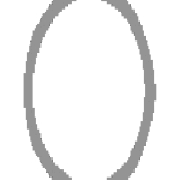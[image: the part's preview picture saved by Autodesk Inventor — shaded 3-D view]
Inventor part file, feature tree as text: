
AUTODESK INVENTOR PART (.ipt)
format: ipt  version: 2021 (Build 250183000, 183)  size: 110,080 bytes
history: native  units: in
note: dims shown in document units (in); Inventor stores cm internally (conversion verified against a paired STEP export)
features: other x4, sketch x3, plane x1
ambient origin geometry x8: Origin, YZ Plane, XZ Plane, XY Plane, X Axis, Y Axis, Z Axis, Center Point
bodies: Solid1 (feature_tree), Body (feature_tree)
feature tree (8):
  other  "Driven Length"
  other  "Frame Generator"
  other  "Start Plane"
  other  "End Plane"
  sketch  "Sketch"  dims[d2=21.5in d4=-0.0in d5=21.5in d6=0.12in d7=0.0in d8=90.0deg d9=21.5in]
  sketch  "Sketch2"  dims[d0=1.0in]
  plane  "Work Plane3"
  sketch  "Sketch3"  dims[d1=0.065in]
